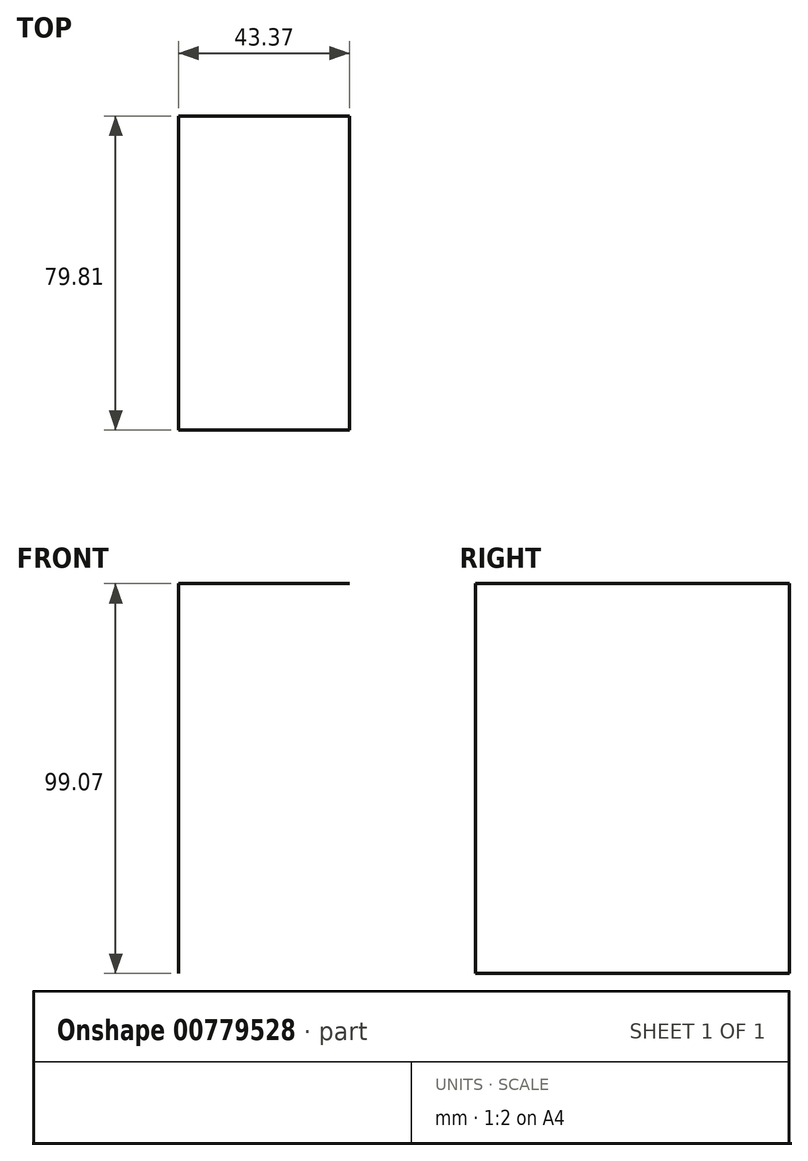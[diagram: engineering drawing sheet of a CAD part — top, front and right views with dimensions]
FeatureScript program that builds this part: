
annotation { "Feature Type Name" : "Feature", "Feature Type Description" : "" }
export const myFeature = defineFeature(function(context is Context, id is Id, definition is map)
    precondition{}
    {
        {
            var Q0;
            Q0=qCreatedBy(makeId("Front.planeOp"),FACE);
            var sketch = newSketch(context, id + "F0", { "sketchPlane" : qUnion([Q0])});
            skLineSegment(sketch, "E0", {"start": v(-58.6, -52.39) * mm, "end": v(-58.6, 46.68) * mm});
            skLineSegment(sketch, "E1", {"start": v(-58.6, 46.68) * mm, "end": v(-15.23, 46.68) * mm});
            skLineSegment(sketch, "E2", {"start": v(-15.23, 46.68) * mm, "end": v(0, 73.57) * mm});
            skLineSegment(sketch, "E3", {"start": v(0, 73.57) * mm, "end": v(0, -52.03) * mm, "construction": true});
            skSolve(sketch);
        }
        {
            var Q0;
            Q0 = qSketchRegion(id + "Fa3kExfWvyL8cO5_0", true);
            var Q1;
            Q1=sQuery(id+"F0.wireOp",EDGE,"E0");
            var Q2;
            Q2=sQuery(id+"F0.wireOp",EDGE,"E1");
            extrude(context, id + "F1", {"entities" : qUnion([Q0]), "bodyType" : ToolBodyType.SURFACE, "surfaceEntities" : qUnion([Q1, Q2]), "depth" : 79.8 * mm, "offsetDistance" : 25.4 * mm});
        }
    });
